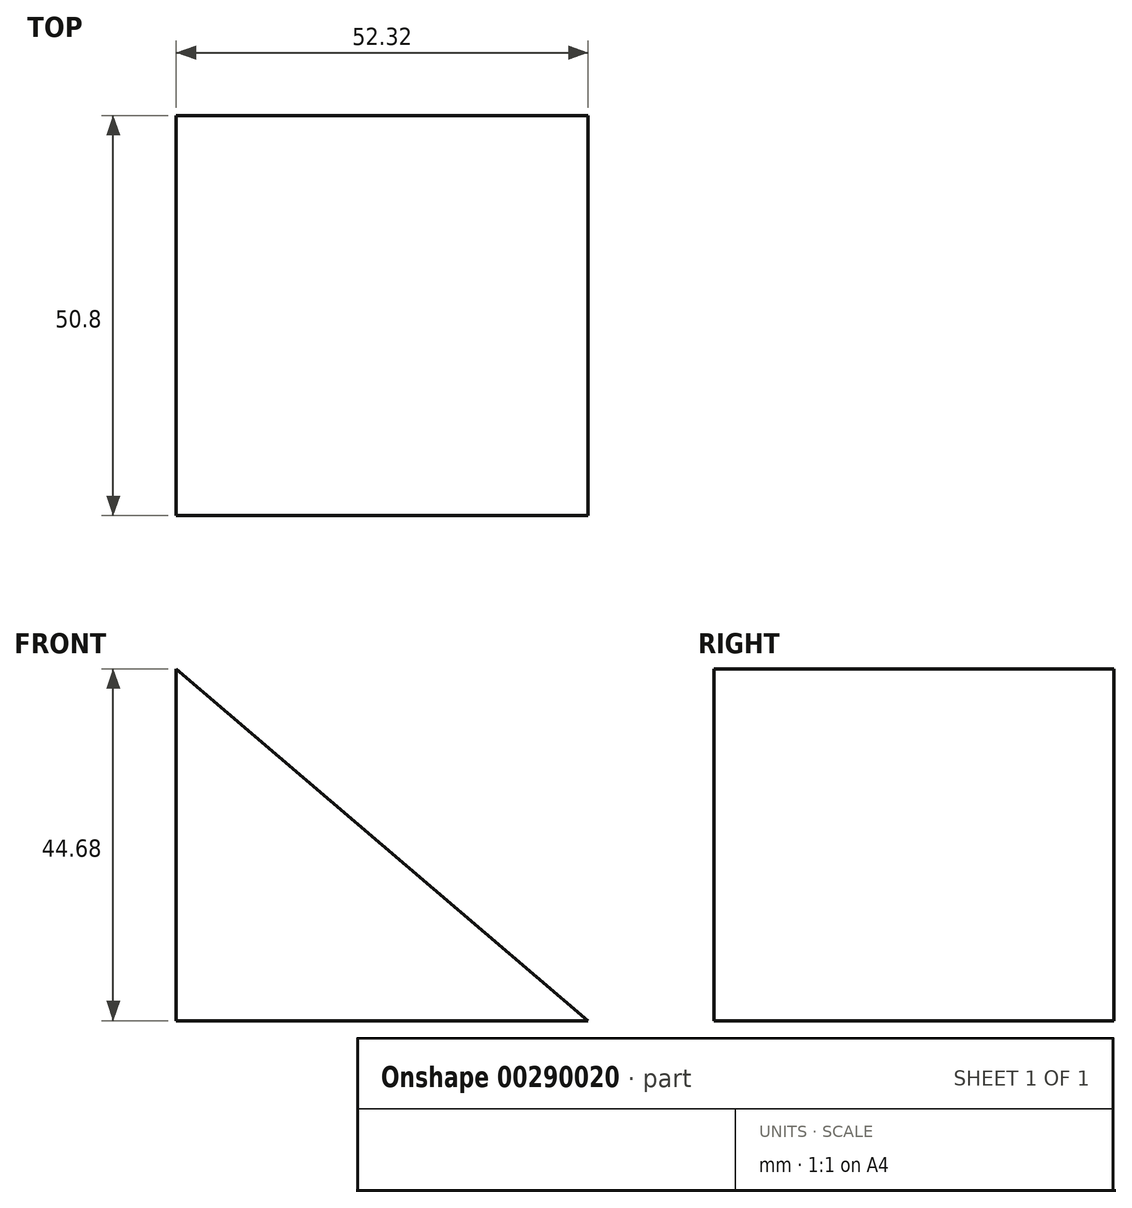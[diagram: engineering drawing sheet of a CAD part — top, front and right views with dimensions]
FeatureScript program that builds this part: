
annotation { "Feature Type Name" : "Feature", "Feature Type Description" : "" }
export const myFeature = defineFeature(function(context is Context, id is Id, definition is map)
    precondition{}
    {
        {
            var Q0;
            Q0=qCreatedBy(makeId("Front.planeOp"),FACE);
            var sketch = newSketch(context, id + "F0", { "sketchPlane" : qUnion([Q0])});
            skLineSegment(sketch, "E0.bottom", {"start": v(0, 0) * mm, "end": v(-52.32, 0) * mm});
            skLineSegment(sketch, "E0.top", {"start": v(0, 44.68) * mm, "end": v(-52.32, 44.68) * mm});
            skLineSegment(sketch, "E0.left", {"start": v(0, 0) * mm, "end": v(0, 44.68) * mm});
            skLineSegment(sketch, "E0.right", {"start": v(-52.32, 0) * mm, "end": v(-52.32, 44.68) * mm});
            skLineSegment(sketch, "E1", {"start": v(-52.32, 44.68) * mm, "end": v(0, 0) * mm});
            skSolve(sketch);
        }
        {
            var Q0;
            Q0=makeQuery(id+"F0.imprint","IMPRINT",FACE,{"disambiguationData":[TD([[makeQuery(id+"F0.imprint","IMPRINT",EDGE,{"derivedFrom":sQuery(id+"F0.wireOp",EDGE,"E0.bottom")}),-1.0]])]});
            extrude(context, id + "F1", {"entities" : qUnion([Q0]), "depth" : 50.8 * mm});
        }
    });
